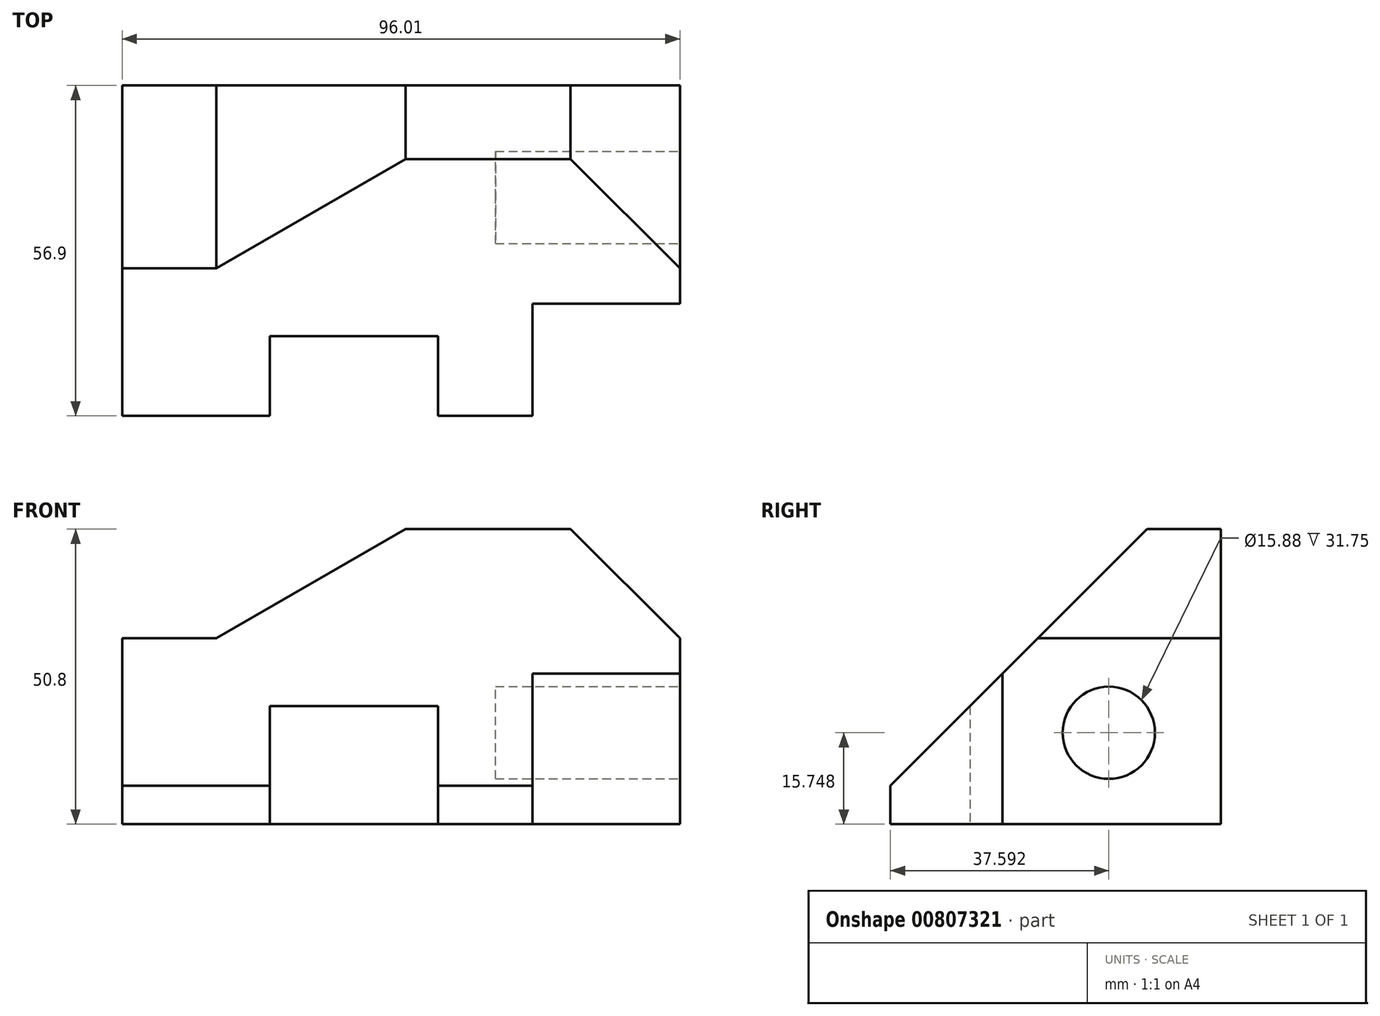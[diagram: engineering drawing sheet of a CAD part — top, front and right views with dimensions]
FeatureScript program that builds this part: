
annotation { "Feature Type Name" : "Feature", "Feature Type Description" : "" }
export const myFeature = defineFeature(function(context is Context, id is Id, definition is map)
    precondition{}
    {
        {
            var Q0;
            Q0=qCreatedBy(makeId("Right.planeOp"),FACE);
            var sketch = newSketch(context, id + "F0", { "sketchPlane" : qUnion([Q0])});
            skLineSegment(sketch, "E0", {"start": v(0, 0) * mm, "end": v(56.9, 0) * mm});
            skLineSegment(sketch, "E1", {"start": v(56.9, 0) * mm, "end": v(56.9, 50.8) * mm});
            skLineSegment(sketch, "E2", {"start": v(56.9, 50.8) * mm, "end": v(44.2, 50.8) * mm});
            skLineSegment(sketch, "E3", {"start": v(44.2, 50.8) * mm, "end": v(0, 6.6) * mm});
            skLineSegment(sketch, "E4", {"start": v(0, 6.6) * mm, "end": v(0, 0) * mm});
            skCircle(sketch, "E5", {"center": v(37.6, 15.75) * mm, "radius": 7.94 * mm});
            skSolve(sketch);
        }
        {
            var Q0;
            Q0=makeQuery(id+"F0.imprint","IMPRINT",FACE,{"disambiguationData":[TD([[makeQuery(id+"F0.imprint","IMPRINT",EDGE,{"derivedFrom":sQuery(id+"F0.wireOp",EDGE,"E0")}),1.0]])]});
            var Q1;
            Q1=makeQuery(id+"F0.imprint","IMPRINT",FACE,{"disambiguationData":[TD([[makeQuery(id+"F0.imprint","IMPRINT",EDGE,{"derivedFrom":sQuery(id+"F0.wireOp",EDGE,"E5")}),1.0]])]});
            extrude(context, id + "F1", {"entities" : qUnion([Q0, Q1]), "oppositeDirection" : true, "depth" : 96.01 * mm, "offsetDistance" : 25.4 * mm});
        }
        {
            var Q0;
            Q0=makeQuery(id+"F0.imprint","IMPRINT",FACE,{"disambiguationData":[TD([[makeQuery(id+"F0.imprint","IMPRINT",EDGE,{"derivedFrom":sQuery(id+"F0.wireOp",EDGE,"E5")}),1.0]])]});
            extrude(context, id + "F2", {"entities" : qUnion([Q0]), "operationType" : NewBodyOperationType.REMOVE, "oppositeDirection" : true, "depth" : 31.75 * mm, "offsetDistance" : 25.4 * mm});
        }
        {
            var Q0;
            Q0=makeQuery(id+"F1.opExtrude","SWEPT_FACE",FACE,{"disambiguationData":[OSD([sQuery(id+"F0.wireOp",EDGE,"E0")])]});
            var sketch = newSketch(context, id + "F3", { "sketchPlane" : qUnion([Q0])});
            skLineSegment(sketch, "E6.0.0", {"start": v(0, -56.9) * mm, "end": v(0, 0) * mm});
            skLineSegment(sketch, "E6.0.1", {"start": v(0, 0) * mm, "end": v(-96.01, 0) * mm});
            skLineSegment(sketch, "E6.0.2", {"start": v(-96.01, 0) * mm, "end": v(-96.01, -56.9) * mm});
            skLineSegment(sketch, "E6.0.3", {"start": v(-96.01, -56.9) * mm, "end": v(0, -56.9) * mm});
            skLineSegment(sketch, "E7", {"start": v(0, -19.3) * mm, "end": v(-25.4, -19.3) * mm});
            skLineSegment(sketch, "E8", {"start": v(-25.4, -19.3) * mm, "end": v(-25.4, 0) * mm});
            skLineSegment(sketch, "E9", {"start": v(-41.66, 0) * mm, "end": v(-41.66, -13.72) * mm});
            skLineSegment(sketch, "E10", {"start": v(-41.66, -13.72) * mm, "end": v(-70.61, -13.72) * mm});
            skLineSegment(sketch, "E11", {"start": v(-70.61, -13.72) * mm, "end": v(-70.61, 0) * mm});
            skSolve(sketch);
        }
        {
            var Q0;
            {var subQ3=sQuery(id+"F3.wireOp",EDGE,"E7");Q0=makeQuery(id+"F3.imprint","IMPRINT",FACE,{"disambiguationData":[TD([[makeQuery(id+"F3.imprint","IMPRINT",EDGE,{"derivedFrom":subQ3}),-1.0]])]});}
            var Q1;
            {var subQ0=sQuery(id+"F3.wireOp",EDGE,"E9");Q1=makeQuery(id+"F3.imprint","IMPRINT",FACE,{"disambiguationData":[TD([[makeQuery(id+"F3.imprint","IMPRINT",EDGE,{"derivedFrom":subQ0}),-1.0]])]});}
            extrude(context, id + "F4", {"entities" : qUnion([Q0, Q1]), "operationType" : NewBodyOperationType.REMOVE, "oppositeDirection" : true, "depth" : 51.56 * mm, "offsetDistance" : 25.4 * mm});
        }
        {
            var Q0;
            Q0=makeQuery(id+"F1.opExtrude","SWEPT_FACE",FACE,{"disambiguationData":[OSD([sQuery(id+"F0.wireOp",EDGE,"E1")])]});
            var sketch = newSketch(context, id + "F5", { "sketchPlane" : qUnion([Q0])});
            skLineSegment(sketch, "E12.0.0", {"start": v(0, 50.8) * mm, "end": v(0, 0) * mm});
            skLineSegment(sketch, "E12.0.1", {"start": v(0, 0) * mm, "end": v(96.01, 0) * mm});
            skLineSegment(sketch, "E12.0.2", {"start": v(96.01, 0) * mm, "end": v(96.01, 50.8) * mm});
            skLineSegment(sketch, "E12.0.3", {"start": v(96.01, 50.8) * mm, "end": v(0, 50.8) * mm});
            skLineSegment(sketch, "E13", {"start": v(0, 32) * mm, "end": v(18.8, 50.8) * mm});
            skLineSegment(sketch, "E14", {"start": v(96.01, 32) * mm, "end": v(79.8, 32) * mm});
            skLineSegment(sketch, "E15", {"start": v(79.8, 32) * mm, "end": v(47.24, 50.8) * mm});
            skSolve(sketch);
        }
        {
            var Q0;
            {var subQ3=sQuery(id+"F5.wireOp",EDGE,"E13");Q0=makeQuery(id+"F5.imprint","IMPRINT",FACE,{"disambiguationData":[TD([[makeQuery(id+"F5.imprint","IMPRINT",EDGE,{"derivedFrom":subQ3}),1.0]])]});}
            var Q1;
            {var subQ3=sQuery(id+"F5.wireOp",EDGE,"E14");Q1=makeQuery(id+"F5.imprint","IMPRINT",FACE,{"disambiguationData":[TD([[makeQuery(id+"F5.imprint","IMPRINT",EDGE,{"derivedFrom":subQ3}),-1.0]])]});}
            extrude(context, id + "F6", {"entities" : qUnion([Q0, Q1]), "operationType" : NewBodyOperationType.REMOVE, "oppositeDirection" : true, "depth" : 69.1 * mm, "offsetDistance" : 25.4 * mm});
        }
    });
